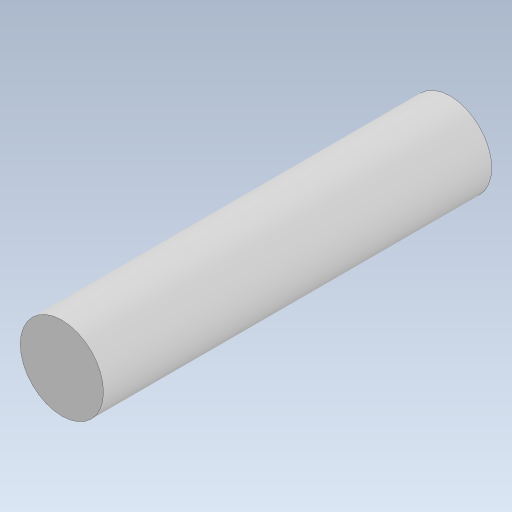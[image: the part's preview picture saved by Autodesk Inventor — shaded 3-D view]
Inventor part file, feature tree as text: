
AUTODESK INVENTOR PART (.ipt)
format: ipt  version: 2023 (Build 270158000, 158)  size: 244,736 bytes
history: native  units: mm
features: extrude x1, sketch x1
ambient origin geometry x8: Origin, YZ Plane, XZ Plane, XY Plane, X Axis, Y Axis, Z Axis, Center Point
bodies: Solid1 (feature_tree)
feature tree (2):
  extrude  "Extrusion1"  Depth=21.0mm TaperAngle=0.0deg
  sketch  "Sketch1"  dims[d0=4.5mm d1=21.0mm d2=0.0mm]
